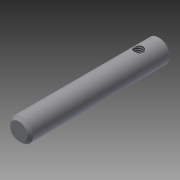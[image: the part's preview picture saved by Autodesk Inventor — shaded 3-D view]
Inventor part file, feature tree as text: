
AUTODESK INVENTOR PART (.ipt)
format: ipt  version: 2015 SP1 (Build 190203100, 203)  size: 93,184 bytes
history: native  units: in
note: dims shown in document units (in); Inventor stores cm internally (conversion verified against a paired STEP export)
features: sketch x2, extrude x1, plane x1, hole x1, chamfer x1
ambient origin geometry x8: Origin, YZ Plane, XZ Plane, XY Plane, X Axis, Y Axis, Z Axis, Center Point
bodies: Body1 (feature_tree)
feature tree (6):
  extrude  "Extrusion5"  Depth=1.9685in TaperAngle=0.0deg
  plane  "Work Plane1"
  hole  "Hole1"  [1 undecoded]
  chamfer  "Chamfer1"  [1 undecoded]
  sketch  "Sketch5"  dims[d17=0.315in d18=1.9685in d19=0.0in]
  sketch  "Sketch7"  dims[d25=0.315in d26=0.1276in d27=0.315in d28=0.1575in d29=0.0787in d30=90.0deg d31=0.4646in d32=0.8108in d33=0.1575in d34=0.0394in d35=0.0787in d36=45.0deg]
note: 2 required parameter values undecoded (feature->parameter linkage not recoverable at this tier; creation-order binding heuristic only, values carry confidence <= 0.55)
